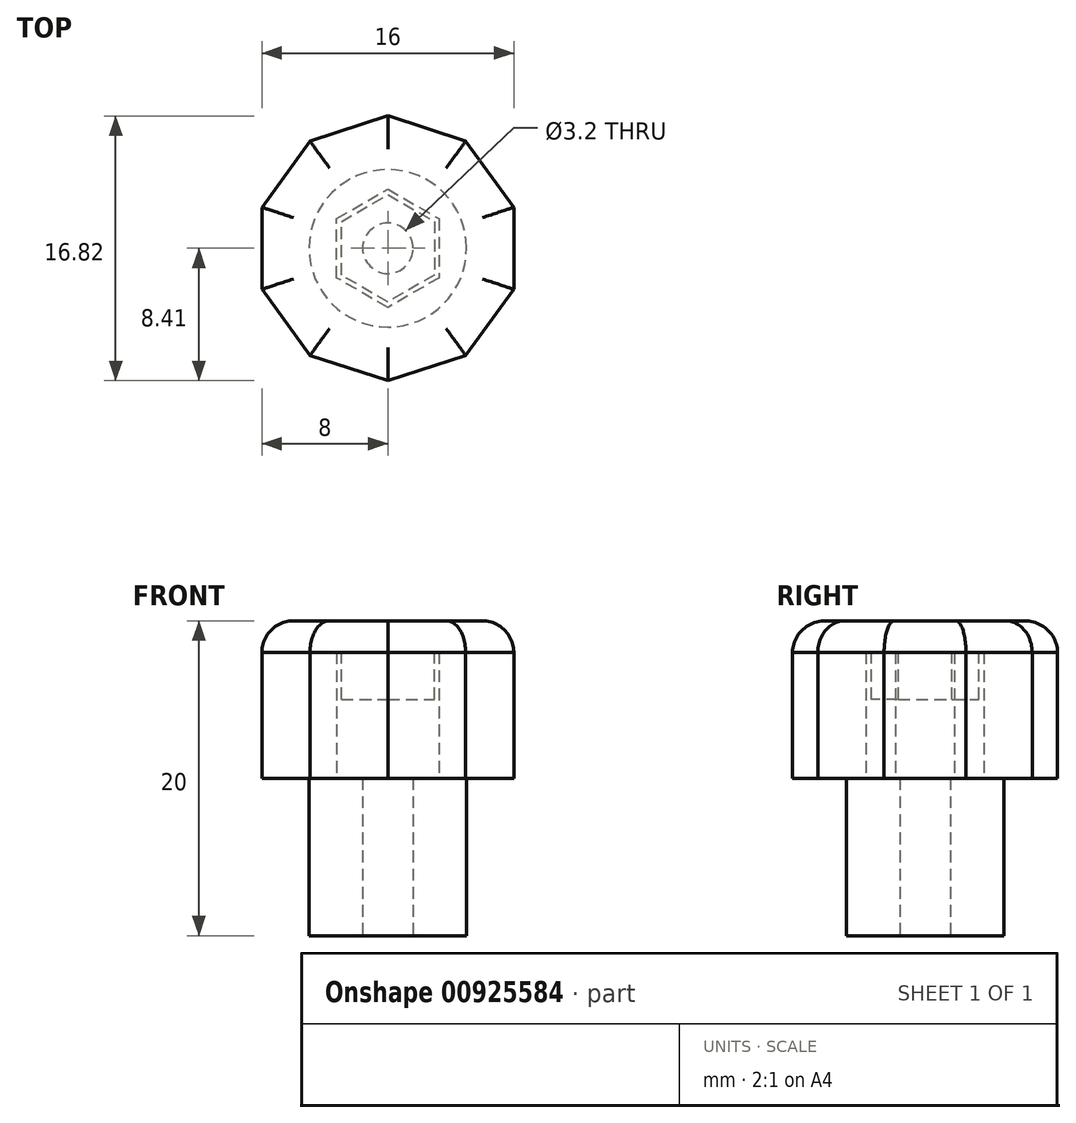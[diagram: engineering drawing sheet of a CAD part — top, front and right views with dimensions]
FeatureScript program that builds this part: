
annotation { "Feature Type Name" : "Feature", "Feature Type Description" : "" }
export const myFeature = defineFeature(function(context is Context, id is Id, definition is map)
    precondition{}
    {
        {
            var Q0;
            Q0=qCreatedBy(makeId("Top.planeOp"),FACE);
            var sketch = newSketch(context, id + "F0", { "sketchPlane" : qUnion([Q0])});
            skCircle(sketch, "E0", {"center": v(0, 0) * mm, "radius": 5 * mm});
            skCircle(sketch, "E1", {"center": v(0, 0) * mm, "radius": 1.6 * mm});
            skSolve(sketch);
        }
        {
            var Q0;
            Q0 = qSketchRegion(id + "F0", true);
            extrude(context, id + "F1", {"entities" : qUnion([Q0]), "depth" : 10 * mm, "offsetDistance" : 25 * mm});
        }
        {
            var Q0;
            Q0=makeQuery(id+"F1.opExtrude","CAP_FACE",FACE,{"disambiguationData":[OSD([sQuery(id+"F0.wireOp",EDGE,"E0"),sQuery(id+"F0.wireOp",EDGE,"E1")])],"isStart":false});
            var sketch = newSketch(context, id + "F2", { "sketchPlane" : qUnion([Q0])});
            skCircle(sketch, "E2.cCircle", {"center": v(0, 0) * mm, "radius": 3.25 * mm, "construction": true});
            skLineSegment(sketch, "E2.0", {"start": v(3.25, 1.88) * mm, "end": v(3.25, -1.88) * mm});
            skLineSegment(sketch, "E2.1", {"start": v(3.25, -1.88) * mm, "end": v(0, -3.75) * mm});
            skLineSegment(sketch, "E2.2", {"start": v(0, -3.75) * mm, "end": v(-3.25, -1.88) * mm});
            skLineSegment(sketch, "E2.3", {"start": v(-3.25, -1.88) * mm, "end": v(-3.25, 1.88) * mm});
            skLineSegment(sketch, "E2.4", {"start": v(-3.25, 1.88) * mm, "end": v(0, 3.75) * mm});
            skLineSegment(sketch, "E2.5", {"start": v(0, 3.75) * mm, "end": v(3.25, 1.88) * mm});
            skPoint(sketch, "E2.0.midPoint", {"position": v(3.25, 0) * mm});
            skCircle(sketch, "E3.cCircle", {"center": v(0, 0) * mm, "radius": 8 * mm, "construction": true});
            skLineSegment(sketch, "E3.0", {"start": v(8, 2.6) * mm, "end": v(8, -2.6) * mm});
            skLineSegment(sketch, "E3.1", {"start": v(8, -2.6) * mm, "end": v(4.94, -6.8) * mm});
            skLineSegment(sketch, "E3.2", {"start": v(4.94, -6.8) * mm, "end": v(0, -8.41) * mm});
            skLineSegment(sketch, "E3.3", {"start": v(0, -8.41) * mm, "end": v(-4.94, -6.8) * mm});
            skLineSegment(sketch, "E3.4", {"start": v(-4.94, -6.8) * mm, "end": v(-8, -2.6) * mm});
            skLineSegment(sketch, "E3.5", {"start": v(-8, -2.6) * mm, "end": v(-8, 2.6) * mm});
            skLineSegment(sketch, "E3.6", {"start": v(-8, 2.6) * mm, "end": v(-4.94, 6.8) * mm});
            skLineSegment(sketch, "E3.7", {"start": v(-4.94, 6.8) * mm, "end": v(0, 8.41) * mm});
            skLineSegment(sketch, "E3.8", {"start": v(0, 8.41) * mm, "end": v(4.94, 6.8) * mm});
            skLineSegment(sketch, "E3.9", {"start": v(4.94, 6.8) * mm, "end": v(8, 2.6) * mm});
            skPoint(sketch, "E3.0.midPoint", {"position": v(8, 0) * mm});
            skSolve(sketch);
        }
        {
            var Q0;
            Q0 = qSketchRegion(id + "F2", true);
            extrude(context, id + "F3", {"entities" : qUnion([Q0]), "operationType" : NewBodyOperationType.ADD, "depth" : 8 * mm, "offsetDistance" : 25 * mm});
        }
        {
            var Q0;
            Q0=makeQuery(id+"F3.opExtrude","CAP_FACE",FACE,{"disambiguationData":[OSD([sQuery(id+"F2.wireOp",EDGE,"E2.0"),sQuery(id+"F2.wireOp",EDGE,"E2.1"),sQuery(id+"F2.wireOp",EDGE,"E2.2"),sQuery(id+"F2.wireOp",EDGE,"E2.3"),sQuery(id+"F2.wireOp",EDGE,"E2.4"),sQuery(id+"F2.wireOp",EDGE,"E2.5"),sQuery(id+"F2.wireOp",EDGE,"E3.0"),sQuery(id+"F2.wireOp",EDGE,"E3.1"),sQuery(id+"F2.wireOp",EDGE,"E3.2"),sQuery(id+"F2.wireOp",EDGE,"E3.3"),sQuery(id+"F2.wireOp",EDGE,"E3.4"),sQuery(id+"F2.wireOp",EDGE,"E3.5"),sQuery(id+"F2.wireOp",EDGE,"E3.6"),sQuery(id+"F2.wireOp",EDGE,"E3.7"),sQuery(id+"F2.wireOp",EDGE,"E3.8"),sQuery(id+"F2.wireOp",EDGE,"E3.9")])],"isStart":false});
            var sketch = newSketch(context, id + "F4", { "sketchPlane" : qUnion([Q0])});
            skLineSegment(sketch, "E4.0", {"start": v(-4.94, 6.8) * mm, "end": v(0, 8.41) * mm});
            skLineSegment(sketch, "E4.1", {"start": v(0, 8.41) * mm, "end": v(4.94, 6.8) * mm});
            skLineSegment(sketch, "E4.2", {"start": v(4.94, 6.8) * mm, "end": v(8, 2.6) * mm});
            skLineSegment(sketch, "E4.3", {"start": v(8, 2.6) * mm, "end": v(8, -2.6) * mm});
            skLineSegment(sketch, "E4.4", {"start": v(8, -2.6) * mm, "end": v(4.94, -6.8) * mm});
            skLineSegment(sketch, "E4.5", {"start": v(4.94, -6.8) * mm, "end": v(0, -8.41) * mm});
            skLineSegment(sketch, "E4.6", {"start": v(0, -8.41) * mm, "end": v(-4.94, -6.8) * mm});
            skLineSegment(sketch, "E4.7", {"start": v(-4.94, -6.8) * mm, "end": v(-8, -2.6) * mm});
            skLineSegment(sketch, "E4.8", {"start": v(-8, -2.6) * mm, "end": v(-8, 2.6) * mm});
            skLineSegment(sketch, "E4.9", {"start": v(-8, 2.6) * mm, "end": v(-4.94, 6.8) * mm});
            skSolve(sketch);
        }
        {
            var Q0;
            Q0 = qSketchRegion(id + "F4", true);
            extrude(context, id + "F5", {"entities" : qUnion([Q0]), "depth" : 2 * mm, "offsetDistance" : 25 * mm});
        }
        {
            var Q0;
            Q0=makeQuery(id+"F5.opExtrude","CAP_FACE",FACE,{"disambiguationData":[OSD([sQuery(id+"F4.wireOp",EDGE,"E4.0"),sQuery(id+"F4.wireOp",EDGE,"E4.1"),sQuery(id+"F4.wireOp",EDGE,"E4.2"),sQuery(id+"F4.wireOp",EDGE,"E4.3"),sQuery(id+"F4.wireOp",EDGE,"E4.4"),sQuery(id+"F4.wireOp",EDGE,"E4.5"),sQuery(id+"F4.wireOp",EDGE,"E4.6"),sQuery(id+"F4.wireOp",EDGE,"E4.7"),sQuery(id+"F4.wireOp",EDGE,"E4.8"),sQuery(id+"F4.wireOp",EDGE,"E4.9")])],"isStart":false});
            fillet(context, id + "F6", {"entities" : qUnion([Q0]), "tangentPropagation" : true, "radius" : 2 * mm, "defaultsChanged" : false, "vertexSettings" : [], "allowEdgeOverflow" : false});
        }
        {
            var Q0;
            Q0=makeQuery(id+"F5.opExtrude","CAP_FACE",FACE,{"disambiguationData":[OSD([sQuery(id+"F4.wireOp",EDGE,"E4.0"),sQuery(id+"F4.wireOp",EDGE,"E4.1"),sQuery(id+"F4.wireOp",EDGE,"E4.2"),sQuery(id+"F4.wireOp",EDGE,"E4.3"),sQuery(id+"F4.wireOp",EDGE,"E4.4"),sQuery(id+"F4.wireOp",EDGE,"E4.5"),sQuery(id+"F4.wireOp",EDGE,"E4.6"),sQuery(id+"F4.wireOp",EDGE,"E4.7"),sQuery(id+"F4.wireOp",EDGE,"E4.8"),sQuery(id+"F4.wireOp",EDGE,"E4.9")])],"isStart":true});
            var sketch = newSketch(context, id + "F7", { "sketchPlane" : qUnion([Q0])});
            skLineSegment(sketch, "E5.0", {"start": v(-3.25, 1.88) * mm, "end": v(-3.25, -1.88) * mm, "construction": true});
            skLineSegment(sketch, "E5.1", {"start": v(-3.25, -1.88) * mm, "end": v(0, -3.75) * mm, "construction": true});
            skLineSegment(sketch, "E5.2", {"start": v(0, 3.75) * mm, "end": v(-3.25, 1.88) * mm, "construction": true});
            skLineSegment(sketch, "E5.3", {"start": v(0, -3.75) * mm, "end": v(3.25, -1.88) * mm, "construction": true});
            skLineSegment(sketch, "E5.4", {"start": v(3.25, -1.88) * mm, "end": v(3.25, 1.88) * mm, "construction": true});
            skLineSegment(sketch, "E5.5", {"start": v(3.25, 1.88) * mm, "end": v(0, 3.75) * mm, "construction": true});
            skLineSegment(sketch, "E6.0", {"start": v(-2.95, 1.7) * mm, "end": v(-2.95, -1.7) * mm});
            skLineSegment(sketch, "E6.1", {"start": v(0, -3.4) * mm, "end": v(2.95, -1.7) * mm});
            skLineSegment(sketch, "E6.2", {"start": v(2.95, -1.7) * mm, "end": v(2.95, 1.7) * mm});
            skLineSegment(sketch, "E6.3", {"start": v(-2.95, -1.7) * mm, "end": v(0, -3.4) * mm});
            skLineSegment(sketch, "E6.4", {"start": v(2.95, 1.7) * mm, "end": v(0, 3.4) * mm});
            skLineSegment(sketch, "E6.5", {"start": v(0, 3.4) * mm, "end": v(-2.95, 1.7) * mm});
            skSolve(sketch);
        }
        {
            var Q0;
            Q0 = qSketchRegion(id + "F7", true);
            extrude(context, id + "F8", {"entities" : qUnion([Q0]), "operationType" : NewBodyOperationType.ADD, "depth" : 3 * mm, "offsetDistance" : 25 * mm});
        }
    });
